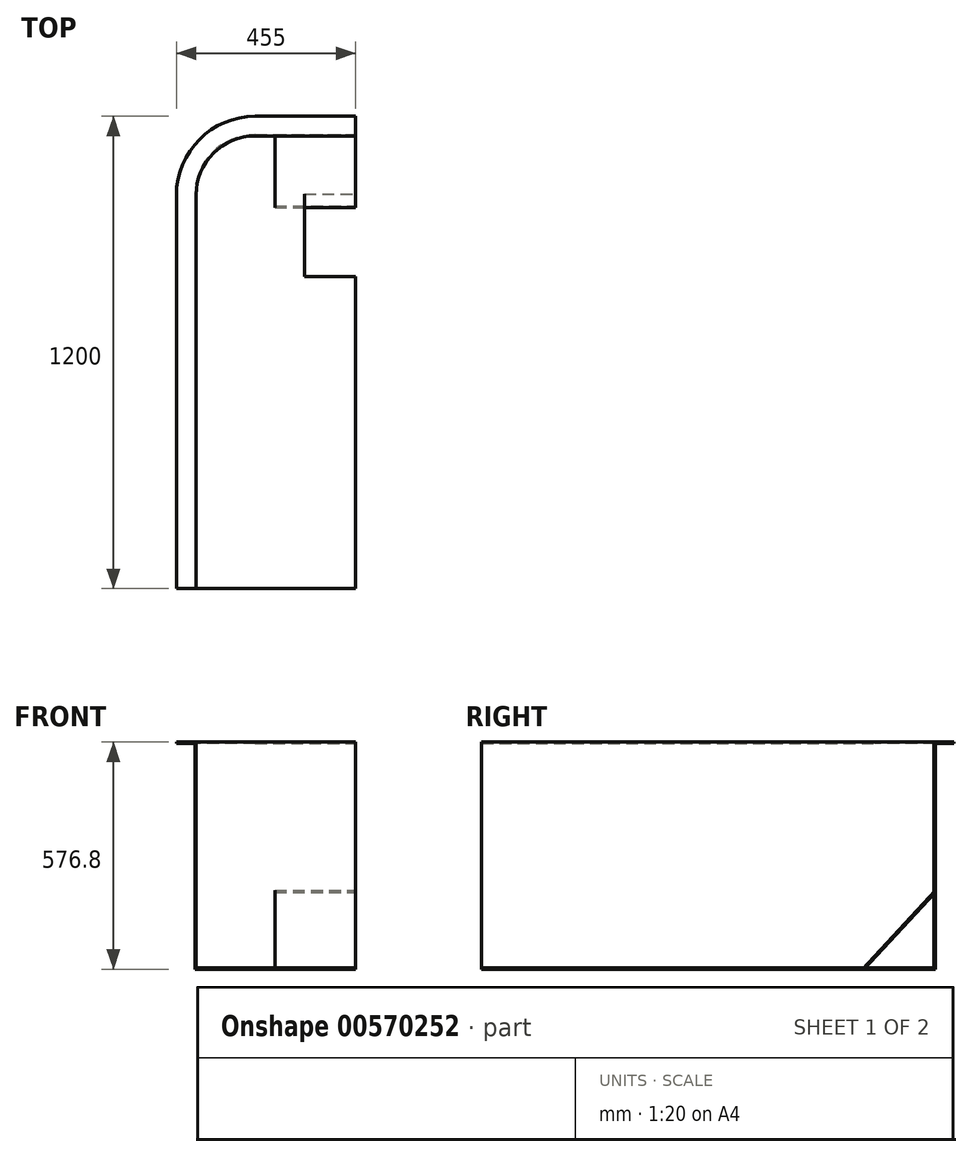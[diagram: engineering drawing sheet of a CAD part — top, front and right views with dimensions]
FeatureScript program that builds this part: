
annotation { "Feature Type Name" : "Feature", "Feature Type Description" : "" }
export const myFeature = defineFeature(function(context is Context, id is Id, definition is map)
    precondition{}
    {
        {
            var Q0;
            Q0=qCreatedBy(makeId("Top.planeOp"),FACE);
            var sketch = newSketch(context, id + "F0", { "sketchPlane" : qUnion([Q0])});
            skLineSegment(sketch, "E0", {"start": v(0, 0) * mm, "end": v(0, 1000) * mm});
            skLineSegment(sketch, "E1.0", {"start": v(0, 1000) * mm, "end": v(50, 1000) * mm});
            skArc(sketch, "E2", {"start": v(200, 1200) * mm, "mid": v(58.58, 1141.42) * mm, "end": v(0, 1000) * mm});
            skArc(sketch, "E3.0", {"start": v(200, 1150) * mm, "mid": v(93.93, 1106.07) * mm, "end": v(50, 1000) * mm});
            skLineSegment(sketch, "E4", {"start": v(50, 1000) * mm, "end": v(50, 0) * mm});
            skLineSegment(sketch, "E5", {"start": v(50, 0) * mm, "end": v(0, 0) * mm});
            skLineSegment(sketch, "E6.trimOffspring", {"start": v(200, 1150) * mm, "end": v(200, 1200) * mm});
            skLineSegment(sketch, "E7", {"start": v(200, 1200) * mm, "end": v(455, 1200) * mm});
            skLineSegment(sketch, "E8", {"start": v(455, 1200) * mm, "end": v(455, 1150) * mm});
            skPoint(sketch, "E9.orphan", {"position": v(455, 1172.43) * mm});
            skLineSegment(sketch, "E10", {"start": v(200, 1150) * mm, "end": v(455, 1150) * mm});
            skSolve(sketch);
        }
        {
            var Q0;
            Q0 = qSketchRegion(id + "F0", true);
            extrude(context, id + "F1", {"entities" : qUnion([Q0]), "depth" : 3.2 * mm, "offsetDistance" : 25.4 * mm});
        }
        {
            var Q0;
            Q0=makeQuery(id+"F1.opExtrude","CAP_FACE",FACE,{"disambiguationData":[OSD([sQuery(id+"F0.wireOp",EDGE,"E0"),sQuery(id+"F0.wireOp",EDGE,"E2"),sQuery(id+"F0.wireOp",EDGE,"E3.0"),sQuery(id+"F0.wireOp",EDGE,"E4"),sQuery(id+"F0.wireOp",EDGE,"E5"),sQuery(id+"F0.wireOp",EDGE,"E7"),sQuery(id+"F0.wireOp",EDGE,"E8"),sQuery(id+"F0.wireOp",EDGE,"E10")])],"isStart":true});
            var sketch = newSketch(context, id + "F2", { "sketchPlane" : qUnion([Q0])});
            skLineSegment(sketch, "E11.0", {"start": v(200, -1153.2) * mm, "end": v(455, -1153.2) * mm});
            skArc(sketch, "E12.0", {"start": v(200, -1153.2) * mm, "mid": v(91.67, -1108.33) * mm, "end": v(46.8, -1000) * mm});
            skLineSegment(sketch, "E13.0", {"start": v(46.8, -1000) * mm, "end": v(46.8, 0) * mm});
            skLineSegment(sketch, "E14", {"start": v(455, -1153.2) * mm, "end": v(455, -1150) * mm});
            skLineSegment(sketch, "E15", {"start": v(455, -1150) * mm, "end": v(200, -1150) * mm});
            skLineSegment(sketch, "E16", {"start": v(46.8, 0) * mm, "end": v(50, 0) * mm});
            skLineSegment(sketch, "E17", {"start": v(50, 0) * mm, "end": v(50, -1000) * mm});
            skArc(sketch, "E18.0", {"start": v(200, -1150) * mm, "mid": v(93.93, -1106.07) * mm, "end": v(50, -1000) * mm});
            skSolve(sketch);
        }
        {
            var Q0;
            Q0 = qSketchRegion(id + "F2", true);
            extrude(context, id + "F3", {"entities" : qUnion([Q0]), "operationType" : NewBodyOperationType.ADD, "depth" : 573.6 * mm, "offsetDistance" : 25.4 * mm});
        }
        {
            var Q0;
            Q0=makeQuery(id+"F3.opExtrude","CAP_FACE",FACE,{"disambiguationData":[OSD([sQuery(id+"F2.wireOp",EDGE,"E11.0"),sQuery(id+"F2.wireOp",EDGE,"E12.0"),sQuery(id+"F2.wireOp",EDGE,"E13.0"),sQuery(id+"F2.wireOp",EDGE,"E14"),sQuery(id+"F2.wireOp",EDGE,"E15"),sQuery(id+"F2.wireOp",EDGE,"E16"),sQuery(id+"F2.wireOp",EDGE,"E17"),sQuery(id+"F2.wireOp",EDGE,"E18.0")])],"isStart":false});
            var sketch = newSketch(context, id + "F4", { "sketchPlane" : qUnion([Q0])});
            skLineSegment(sketch, "E19", {"start": v(455, -1150) * mm, "end": v(455, -1003) * mm});
            skLineSegment(sketch, "E20", {"start": v(50, 0) * mm, "end": v(455, 0) * mm});
            skLineSegment(sketch, "E21", {"start": v(455, -793) * mm, "end": v(325, -793) * mm});
            skLineSegment(sketch, "E22", {"start": v(325, -793) * mm, "end": v(325, -1003) * mm});
            skLineSegment(sketch, "E23", {"start": v(325, -1003) * mm, "end": v(455, -1003) * mm});
            skLineSegment(sketch, "E24.trimOffspring", {"start": v(455, -793) * mm, "end": v(455, 0) * mm});
            skSolve(sketch);
        }
        {
            var Q0;
            Q0 = qSketchRegion(id + "F4", true);
            var Q1;
            Q1=makeQuery(id+"F4.imprint","IMPRINT",FACE,{"disambiguationData":[TD([[makeQuery(id+"F4.imprint","IMPRINT",EDGE,{"derivedFrom":sQuery(id+"F4.wireOp",EDGE,"E19")}),1.0]])]});
            extrude(context, id + "F5", {"entities" : qUnion([Q0, Q1]), "oppositeDirection" : true, "depth" : 3.2 * mm, "offsetDistance" : 25.4 * mm});
        }
        {
            var Q0;
            Q0=makeQuery(id+"F3.boolean.opBoolean","MERGE",FACE,{"derivedFrom":[makeQuery(id+"F1.opExtrude","SWEPT_FACE",FACE,{"disambiguationData":[OSD([sQuery(id+"F0.wireOp",EDGE,"E8")])]}),makeQuery(id+"F3.opExtrude","SWEPT_FACE",FACE,{"disambiguationData":[OSD([sQuery(id+"F2.wireOp",EDGE,"E14")])]})]});
            var sketch = newSketch(context, id + "F6", { "sketchPlane" : qUnion([Q0])});
            skLineSegment(sketch, "E25.0", {"start": v(1150, -378.6) * mm, "end": v(1003, -378.6) * mm});
            skLineSegment(sketch, "E26.0", {"start": v(972.2, -573.6) * mm, "end": v(972.2, 0) * mm});
            skLineSegment(sketch, "E27", {"start": v(1150, -378.6) * mm, "end": v(1153.2, -378.6) * mm});
            skLineSegment(sketch, "E28", {"start": v(972.2, -573.6) * mm, "end": v(1153.2, -378.6) * mm});
            skLineSegment(sketch, "E29.0", {"start": v(967.83, -573.6) * mm, "end": v(1153.2, -373.9) * mm});
            skLineSegment(sketch, "E30", {"start": v(1153.2, -378.6) * mm, "end": v(1153.2, -373.9) * mm});
            skLineSegment(sketch, "E31", {"start": v(972.2, -573.6) * mm, "end": v(967.83, -573.6) * mm});
            skSolve(sketch);
        }
        {
            var Q0;
            Q0 = qSketchRegion(id + "F6", true);
            extrude(context, id + "F7", {"entities" : qUnion([Q0]), "oppositeDirection" : true, "depth" : 205 * mm, "offsetDistance" : 25.4 * mm});
        }
    });
